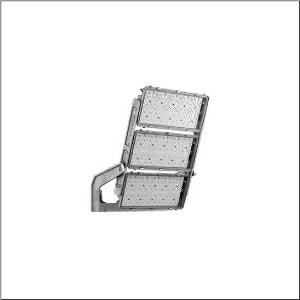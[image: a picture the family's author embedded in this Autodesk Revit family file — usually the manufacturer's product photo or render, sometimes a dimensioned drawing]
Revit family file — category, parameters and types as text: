
# Revit family: floodlight_fl_11_maxi_pro_remote___pl64_5xa779524e01aa_eec4
name_source: partatom
category: Lighting Fixtures
units: mm (PartAtom-declared; Revit-internal decimal feet)

## family parameters
Cut with Voids When Loaded = No
Host = Face
Light Source = No
Part Type = Normal
Room Calculation Point = No
Round Connector Dimension = Use Diameter
Shared = No

## types (1)
- --- (1 x LED, 128450 lm, 1334.7 W, 5700K)
    Apparent Load = 1335 VA
    CIE Flux Codes = 28 80 98 100 100
    Color Rendering = 90
    Color Temperature = 5700K
    Default Elevation = 1800 mm
    Description = Floodlight FL 11  maxi  pro Remote floodlight; light control with lens of PMMA; cover panel of toughened safety glass, transparent; light distribution: PL64, asymmetric direct distribution, LEDcolour temperature: 5700K, rated luminous flux: 128.450lm, colour rendering: CRI > 90, light colour: 957; luminous efficacy: 96lm/W; brightness control: DMX+RDM; with terminal, 6-pole, max. 2.5mm², mains connection: 220..240V/380..400V AC, 50/60Hz, surge voltage resistance: line to ground: 10kV, ECG replaceable separately, no afterglow with DALI off / DMX off command, LED unit replaceable without ESD environment, dustproof LED module, dimming range 10..100%; 1335W floodlight with 3x LED unit of diecast aluminium, coated grey; length: 713mm / width: 651mm / height: 338mm; mounting bracket, of diecast aluminium, uncoated, natural, equipment: Power, protection rating (complete): IP66; insulation class (complete): insulation class I (protective earthing); certification: CE, ENEC, VDE; ball protection: ball impact resistance with accessories, impact resistance: IK07; only for outdoor installations, rated ambient temperature 10°C, permissible operating ambient temperature: -40..+30°C, permissible storage temperature: -40..+85°Cpackaging unit: 1 piece

Light Distribution: PL64
    Height = 320 mm
    Lamp = 1 x LED
    Lamp Light Flux = 128450 lm
    Lamp Power = 1334.7 W
    Lamp count = 1
    Length = 1002 mm
    Luminous efficacy = 96 lm/W
    Manufacturer = Siteco
    ModVariant = No
    Model = 5XA779524E01AA
    Mounting Place = Ceiling
    Mounting Type = Surface mounted
    Number of Poles = 1
    OnlyDefault = Yes
    Power Factor = 1
    Product Name = Floodlight FL 11 maxi pro Remote | PL64
    Product group = floodlight | ceiling mounted
    ProductGroupID = 301
    Protection Class = Protection class I
    Protection Degree = IP 66
    RLX_Detail_Level = 1
    RLX_Emergency_Light_Flux = 0 lm
    RLX_Emergency_Type = 0
    RLX_Emergency_Type_DB = No
    RlxData = <blob elided: 52341 chars, md5=7981cf73>
    Socket = socket
    Standby Power = 0 W
    System Light Flux = 128450 lm
    System Power = 1335 W
    Type Comments = factory setting: luminous flux: 100 % | dim-lin: 255 | 920 mA
    Type Image = l_1349141.jpg
    URL = http://relux.com
    VarID = @adj_097314
    Voltage = 0 V
    Weight = 0.00 kg
    Width = 655 mm

## geometry (parser evidence)
native form markers: Blend x4, Sweep x14
no freeform markers — native parametric forms only
